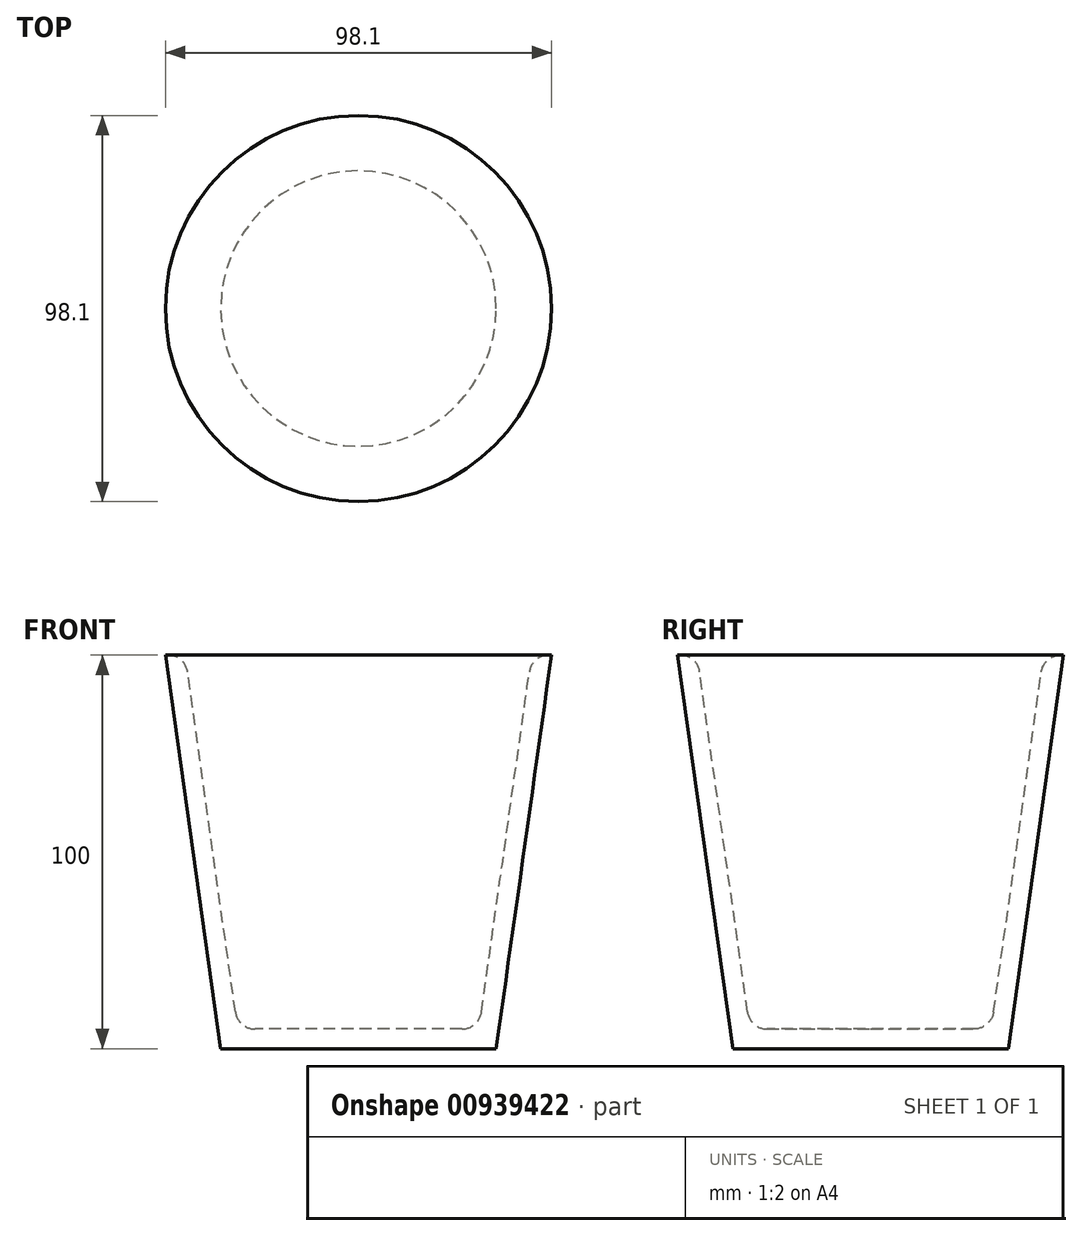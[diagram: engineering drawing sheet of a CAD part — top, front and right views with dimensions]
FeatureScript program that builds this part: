
annotation { "Feature Type Name" : "Feature", "Feature Type Description" : "" }
export const myFeature = defineFeature(function(context is Context, id is Id, definition is map)
    precondition{}
    {
        {
            var Q0;
            Q0=qCreatedBy(makeId("Top.planeOp"),FACE);
            var sketch = newSketch(context, id + "F0", { "sketchPlane" : qUnion([Q0])});
            skCircle(sketch, "E0", {"center": v(0, 0) * mm, "radius": 35 * mm});
            skSolve(sketch);
        }
        {
            var Q0;
            Q0 = qSketchRegion(id + "F0", true);
            extrude(context, id + "F1", {"entities" : qUnion([Q0]), "depth" : 100 * mm, "offsetDistance" : 25 * mm, "hasDraft" : true, "draftAngle" : 8 * degree});
        }
        {
            var Q0;
            Q0=makeQuery(id+"F1.opExtrude","CAP_FACE",FACE,{"disambiguationData":[OSD([sQuery(id+"F0.wireOp",EDGE,"E0")])],"isStart":false});
            shell(context, id + "F2", {"entities" : qUnion([Q0]), "thickness" : 5 * mm});
        }
        {
            var Q0;
            {var subQ0=sQuery(id+"F0.wireOp",EDGE,"E0");Q0=makeQuery(id+"F2.opShell","OFFSET_EDGE",EDGE,{"disambiguationData":[OSD([subQ0]),TDD([makeQuery(id+"F1.opExtrude","CAP_EDGE",EDGE,{"disambiguationData":[OSD([subQ0])],"isStart":false})])]});}
            var Q1;
            {var subQ0=sQuery(id+"F0.wireOp",EDGE,"E0");Q1=makeQuery(id+"F2.opShell","OFFSET_FACE",FACE,{"disambiguationData":[OSD([subQ0]),TDD([makeQuery(id+"F1.opExtrude","CAP_FACE",FACE,{"disambiguationData":[OSD([subQ0])],"isStart":true})])]});}
            fillet(context, id + "F3", {"entities" : qUnion([Q0, Q1]), "radius" : 5 * mm, "tangentPropagation" : true, "allowEdgeOverflow" : false});
        }
    });
